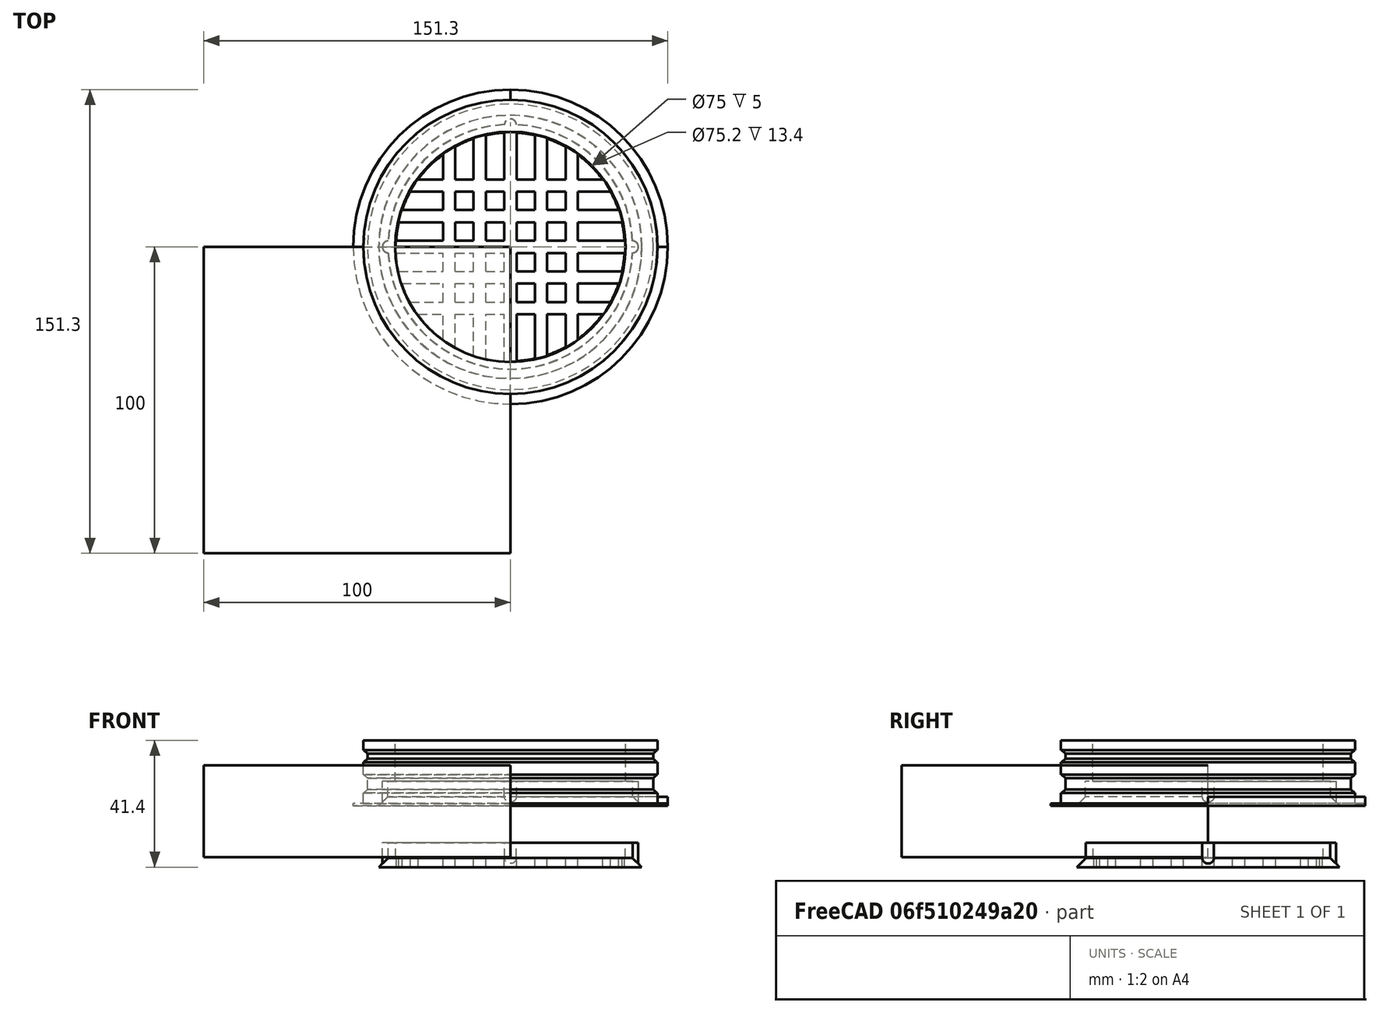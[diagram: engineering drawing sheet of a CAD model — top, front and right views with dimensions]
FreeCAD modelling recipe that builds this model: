
FCSTD DOCUMENT  (FreeCAD 0.18R4 (GitTag))
Label: rejilla_banio_20
License: CreativeCommons Attribution-ShareAlike
LicenseURL: http://creativecommons.org/licenses/by-sa/4.0/
objects: Part::Cylinder×30, Part::Cut×18, Part::Box×12, Part::MultiFuse×10, Part::Cone×2, Part::Chamfer×2
note: 74 computed .brp shape members not serialized (recipe doc carries the construction recipe); baked Part::Feature solids carry a one-line shape summary decoded from their .brp

FEATURE [Part::Cylinder] Cylinder
  Angle = 360
  AttacherType = Attacher::AttachEngine3D
  Height = 3.2
  Radius = 48
FEATURE [Part::Cylinder] Cylinder001
  Angle = 360
  AttacherType = Attacher::AttachEngine3D
  Height = 4
  Placement = pos=(0,0,-4) rot=(0,0,1;0rad)
  Radius = 46.6
FEATURE [Part::Cylinder] Cylinder002
  Angle = 360
  AttacherType = Attacher::AttachEngine3D
  Height = 4
  Placement = pos=(0,0,-8) rot=(0,0,1;0rad)
  Radius = 48
FEATURE [Part::Cylinder] Cylinder003
  Angle = 360
  AttacherType = Attacher::AttachEngine3D
  Height = 6
  Placement = pos=(0,0,-14) rot=(0,0,1;0rad)
  Radius = 46.6
FEATURE [Part::Cylinder] Cylinder004
  Angle = 360
  AttacherType = Attacher::AttachEngine3D
  Height = 1.2
  Placement = pos=(0,0,-15.2) rot=(0,0,1;0rad)
  Radius = 48
FEATURE [Part::MultiFuse] Fusion
  Shapes = -> [Cylinder004,Cylinder,Cylinder003,Cylinder001,Cylinder002]
FEATURE [Part::Cylinder] Cylinder005
  Angle = 360
  AttacherType = Attacher::AttachEngine3D
  Height = 25
  Placement = pos=(0,0,-18) rot=(0,0,1;0rad)
  Radius = 45
FEATURE [Part::Cut] Cut
  Base = -> Fusion
  Tool = -> Cylinder005
FEATURE [Part::Cylinder] Cylinder006  label="ajustar_radio_de_este"
  Angle = 360
  AttacherType = Attacher::AttachEngine3D
  Height = 5
  Placement = pos=(0,0,-20.2) rot=(0,0,1;0rad)
  Radius = 51.3
FEATURE [Part::Cylinder] Cylinder007
  Angle = 360
  AttacherType = Attacher::AttachEngine3D
  Height = 25
  Placement = pos=(0,0,-23) rot=(0,0,1;0rad)
  Radius = 45
FEATURE [Part::Cut] Cut001
  Base = -> Cylinder006
  Tool = -> Cylinder007
FEATURE [Part::MultiFuse] Fusion001
  Shapes = -> [Cut001,Cut]
FEATURE [Part::Cone] Cone
  Angle = 360
  AttacherType = Attacher::AttachEngine3D
  Height = 5
  Placement = pos=(0,0,-15.2) rot=(0,1,0;3.14159rad)
  Radius1 = 40
  Radius2 = 45
FEATURE [Part::Cylinder] Cylinder008
  Angle = 360
  AttacherType = Attacher::AttachEngine3D
  Height = 23.4
  Placement = pos=(0,0,-20.2) rot=(0,0,1;0rad)
  Radius = 45
FEATURE [Part::Cylinder] Cylinder009
  Angle = 360
  AttacherType = Attacher::AttachEngine3D
  Height = 27.4
  Placement = pos=(0,0,-17) rot=(0,0,1;0rad)
  Radius = 40
FEATURE [Part::MultiFuse] Fusion002
  Shapes = -> [Cylinder009,Cone]
FEATURE [Part::Cut] Cut002
  Base = -> Cylinder008
  Tool = -> Fusion002
FEATURE [Part::MultiFuse] Fusion003  label="rejilla_sin_cortar_oblicuo_sin_chaflan"
  Shapes = -> [Fusion001,Cut002]
FEATURE [Part::Chamfer] Chamfer
  Base = -> Fusion003
  Edges = 2 edges r=1.2: [Edge12,Edge24]
FEATURE [Part::Chamfer] Chamfer001  label="rejilla__exteriorsin_cortar_oblicuo_alta"
  Base = -> Chamfer
  Edges = 2 edges r=1.2: [Edge8,Edge26]
FEATURE [Part::Cylinder] Cylinder019  label="ajustar_radio_de_este001"
  Angle = 360
  AttacherType = Attacher::AttachEngine3D
  Height = 5
  Placement = pos=(0,0,-23.2) rot=(0,0,1;0rad)
  Radius = 68.3
FEATURE [Part::Cut] Cut009  label="rejilla__exterior_sin_cortar_oblicuo_sin_muescas_01"
  Base = -> Chamfer001
  Tool = -> Cylinder019
FEATURE [Part::Cylinder] Cylinder042
  Angle = 360
  AttacherType = Attacher::AttachEngine3D
  Height = 5
  Radius = 37.5
FEATURE [Part::Cylinder] Cylinder043
  Angle = 360
  AttacherType = Attacher::AttachEngine3D
  Height = 5
  Radius = 39.9
FEATURE [Part::Cut] Cut021
  Base = -> Cylinder043
  Placement = pos=(0,0,-15.2) rot=(0,0,1;0rad)
  Tool = -> Cylinder042
FEATURE [Part::Cone] Cone003
  Angle = 360
  AttacherType = Attacher::AttachEngine3D
  Height = 5
  Placement = pos=(0,0,-15.2) rot=(0,1,0;3.14159rad)
  Radius1 = 39.85
  Radius2 = 44.9
FEATURE [Part::Cylinder] Cylinder044
  Angle = 360
  AttacherType = Attacher::AttachEngine3D
  Height = 10
  Placement = pos=(0,0,-49) rot=(0,0,1;0rad)
  Radius = 50
FEATURE [Part::Box] Box010  label="Cube010"
  AttacherType = Attacher::AttachEngine3D
  Height = 5
  Length = 74
  Placement = pos=(12,-37,-41) rot=(0,0,1;1.5708rad)
  Width = 4
FEATURE [Part::Box] Box011  label="Cube011"
  AttacherType = Attacher::AttachEngine3D
  Height = 5
  Length = 66
  Placement = pos=(-33,-22,-41) rot=(0,0,1;0rad)
  Width = 4
FEATURE [Part::Box] Box012  label="Cube012"
  AttacherType = Attacher::AttachEngine3D
  Height = 5
  Length = 66
  Placement = pos=(22,-33,-41) rot=(0,0,1;1.5708rad)
  Width = 4
FEATURE [Part::Box] Box013  label="Cube013"
  AttacherType = Attacher::AttachEngine3D
  Height = 5
  Length = 66
  Placement = pos=(-18,-33,-41) rot=(0,0,1;1.5708rad)
  Width = 4
FEATURE [Part::Cylinder] Cylinder045
  Angle = 360
  AttacherType = Attacher::AttachEngine3D
  Height = 7.8
  Placement = pos=(-39.8,0,-18) rot=(0,0,1;0rad)
  Radius = 1.9
FEATURE [Part::Box] Box014  label="Cube014"
  AttacherType = Attacher::AttachEngine3D
  Height = 5
  Length = 76
  Placement = pos=(-38,-2,-41) rot=(0,0,1;0rad)
  Width = 4
FEATURE [Part::Box] Box015  label="Cube015"
  AttacherType = Attacher::AttachEngine3D
  Height = 5
  Length = 74
  Placement = pos=(-8,-37,-41) rot=(0,0,1;1.5708rad)
  Width = 4
FEATURE [Part::Cylinder] Cylinder046
  Angle = 360
  AttacherType = Attacher::AttachEngine3D
  Height = 5
  Placement = pos=(0,0,-41) rot=(0,0,1;0rad)
  Radius = 45
FEATURE [Part::Cylinder] Cylinder047
  Angle = 360
  AttacherType = Attacher::AttachEngine3D
  Height = 7.8
  Placement = pos=(39.8,0,-18) rot=(0,0,1;0rad)
  Radius = 1.9
FEATURE [Part::Cylinder] Cylinder048
  Angle = 360
  AttacherType = Attacher::AttachEngine3D
  Height = 5
  Placement = pos=(0,0,-41) rot=(0,0,1;0rad)
  Radius = 37.5
FEATURE [Part::Box] Box016  label="Cube016"
  AttacherType = Attacher::AttachEngine3D
  Height = 5
  Length = 74
  Placement = pos=(-37,8,-41) rot=(0,0,1;0rad)
  Width = 4
FEATURE [Part::Box] Box017  label="Cube017"
  AttacherType = Attacher::AttachEngine3D
  Height = 5
  Length = 66
  Placement = pos=(-33,18,-41) rot=(0,0,1;0rad)
  Width = 4
FEATURE [Part::Cylinder] Cylinder049
  Angle = 360
  AttacherType = Attacher::AttachEngine3D
  Height = 5
  Placement = pos=(0,0,-41) rot=(0,0,1;0rad)
  Radius = 37.5
FEATURE [Part::Cut] Cut020
  Base = -> Cylinder046
  Tool = -> Cylinder049
FEATURE [Part::Box] Box018  label="Cube018"
  AttacherType = Attacher::AttachEngine3D
  Height = 5
  Length = 74
  Placement = pos=(-37,-12,-41) rot=(0,0,1;0rad)
  Width = 4
FEATURE [Part::Cylinder] Cylinder050  label="ajustar_radio_de_este005"
  Angle = 360
  AttacherType = Attacher::AttachEngine3D
  Height = 5
  Placement = pos=(0,0,-23.2) rot=(0,0,1;0rad)
  Radius = 68.3
FEATURE [Part::Cylinder] Cylinder051
  Angle = 360
  AttacherType = Attacher::AttachEngine3D
  Height = 32
  Placement = pos=(0,0,-39) rot=(0,0,1;0rad)
  Radius = 37.5
FEATURE [Part::Cut] Cut019
  Base = -> Cone003
  Tool = -> Cylinder051
FEATURE [Part::MultiFuse] Fusion015  label="rejilla_interior_sin_cortar_oblicuo_sin_tapa_006"
  Shapes = -> [Cut021,Cut019]
FEATURE [Part::Box] Box019  label="Cube019"
  AttacherType = Attacher::AttachEngine3D
  Height = 5
  Length = 76
  Placement = pos=(2,-38,-41) rot=(0,0,1;1.5708rad)
  Width = 4
FEATURE [Part::Cylinder] Cylinder052
  Angle = 360
  AttacherType = Attacher::AttachEngine3D
  Height = 5
  Placement = pos=(0,0,-41) rot=(0,0,1;0rad)
  Radius = 37.3
FEATURE [Part::Cut] Cut022  label="anillo001"
  Base = -> Cylinder048
  Tool = -> Cylinder052
FEATURE [Part::MultiFuse] Fusion016
  Shapes = -> [Cut022,Box013,Box012,Box015,Box016,Box018,Box011,Box014,Box017,Box019,Box010]
FEATURE [Part::Cut] Cut023
  Base = -> Fusion016
  Tool = -> Cut020
FEATURE [Part::Cut] Cut024
  Base = -> Cut023
  Placement = pos=(0,0,20.8) rot=(0,0,1;0rad)
  Tool = -> Cylinder044
FEATURE [Part::Cut] Cut025
  Base = -> Fusion015
  Tool = -> Cylinder050
FEATURE [Part::MultiFuse] Fusion017  label="rejilla__interior_sin_cortar_oblicuo_sin_muescas001"
  Shapes = -> [Cut024,Cut025]
FEATURE [Part::MultiFuse] Fusion014  label="rejilla__interior_sin_cortar_oblicuo001"
  Shapes = -> [Fusion017,Cylinder045,Cylinder047]
FEATURE [Part::Cylinder] Cylinder053
  Angle = 360
  AttacherType = Attacher::AttachEngine3D
  Height = 7.8
  Placement = pos=(0,39.8,-18) rot=(0,0,1;0rad)
  Radius = 1.9
FEATURE [Part::MultiFuse] Fusion018  label="rejilla__interior_v2.0_cono_39.85"
  Shapes = -> [Fusion014,Cylinder053]
FEATURE [Part::Cylinder] Cylinder054
  Angle = 360
  AttacherType = Attacher::AttachEngine3D
  Height = 7.8
  Placement = pos=(0,39.8,-18) rot=(0,0,1;0rad)
  Radius = 2
FEATURE [Part::Cylinder] Cylinder055
  Angle = 360
  AttacherType = Attacher::AttachEngine3D
  Height = 13.4
  Placement = pos=(0,0,-10.2) rot=(0,0,1;0rad)
  Radius = 40
FEATURE [Part::Cylinder] Cylinder056
  Angle = 360
  AttacherType = Attacher::AttachEngine3D
  Height = 13.4
  Placement = pos=(0,0,-10.2) rot=(0,0,1;0rad)
  Radius = 37.6
FEATURE [Part::Cut] Cut026
  Base = -> Cylinder055
  Tool = -> Cylinder056
FEATURE [Part::MultiFuse] Fusion019  label="rejilla__exterior_sin_cortar_oblicuo_sin_muescas"
  Shapes = -> [Cut009,Cut026]
FEATURE [Part::Cylinder] Cylinder057
  Angle = 360
  AttacherType = Attacher::AttachEngine3D
  Height = 7.8
  Placement = pos=(39.8,0,-18) rot=(0,0,1;0rad)
  Radius = 2
FEATURE [Part::Cylinder] Cylinder058
  Angle = 360
  AttacherType = Attacher::AttachEngine3D
  Height = 7.8
  Placement = pos=(-39.8,0,-18) rot=(0,0,1;0rad)
  Radius = 2
FEATURE [Part::Cut] Cut027
  Base = -> Fusion019
  Tool = -> Cylinder054
FEATURE [Part::Cut] Cut028
  Base = -> Cut027
  Tool = -> Cylinder057
FEATURE [Part::Cut] Cut029  label="rejilla__exterior_sin_cortar"
  Base = -> Cut028
  Tool = -> Cylinder058
FEATURE [Part::Cylinder] Cylinder059  label="ajustar_radio_de_este006"
  Angle = 360
  AttacherType = Attacher::AttachEngine3D
  Height = 2.28
  Placement = pos=(0,0,-20.2) rot=(0,0,1;0rad)
  Radius = 51.3
FEATURE [Part::Cylinder] Cylinder060
  Angle = 360
  AttacherType = Attacher::AttachEngine3D
  Height = 7
  Placement = pos=(0,0,-21.2) rot=(0,0,1;0rad)
  Radius = 48
FEATURE [Part::Cut] Cut030
  Base = -> Cylinder059
  Tool = -> Cylinder060
FEATURE [Part::Box] Box  label="Cube"
  AttacherType = Attacher::AttachEngine3D
  Height = 20
  Length = 70
  Placement = pos=(0,0,-24) rot=(0,0,1;0rad)
  Width = 70
FEATURE [Part::Cut] Cut031
  Base = -> Cut030
  Placement = pos=(0,0,2.72) rot=(0,0,1;0rad)
  Tool = -> Box
FEATURE [Part::Cut] Cut032  label="rejilla__exterior_sin_cortar_v20_beta"
  Base = -> Cut029
  Placement = pos=(0,0,20) rot=(0,0,1;0rad)
  Tool = -> Cut031
FEATURE [Part::Box] Box021  label="Cube021"
  AttacherType = Attacher::AttachEngine3D
  Height = 30
  Length = 100
  Placement = pos=(-100,-100,-15) rot=(0,0,1;0rad)
  Width = 100
